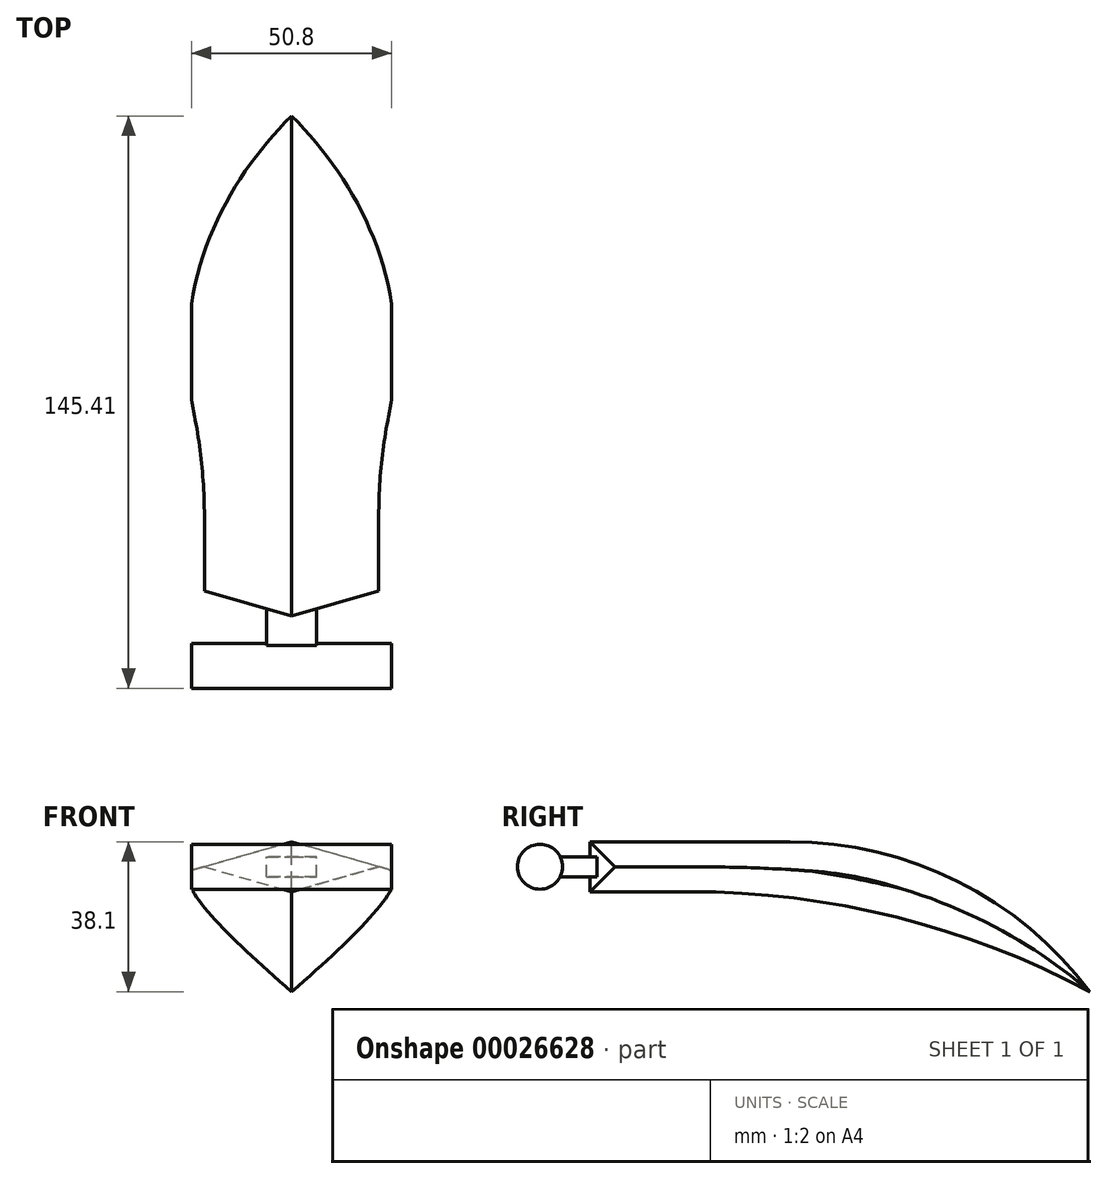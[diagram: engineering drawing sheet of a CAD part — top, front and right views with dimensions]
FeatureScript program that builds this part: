
annotation { "Feature Type Name" : "Feature", "Feature Type Description" : "" }
export const myFeature = defineFeature(function(context is Context, id is Id, definition is map)
    precondition{}
    {
        {
            var Q0;
            Q0=qCreatedBy(makeId("Front.planeOp"),FACE);
            var sketch = newSketch(context, id + "F0", { "sketchPlane" : qUnion([Q0])});
            skLineSegment(sketch, "E0.bottom", {"start": v(0, 0) * mm, "end": v(50.8, 0) * mm});
            skLineSegment(sketch, "E0.top", {"start": v(0, 50.8) * mm, "end": v(50.8, 50.8) * mm});
            skLineSegment(sketch, "E0.left", {"start": v(0, 0) * mm, "end": v(0, 50.8) * mm});
            skLineSegment(sketch, "E0.right", {"start": v(50.8, 0) * mm, "end": v(50.8, 50.8) * mm});
            skSolve(sketch);
        }
        {
            var Q0;
            Q0=qSketchRegion(id+"F0",true);
            extrude(context, id + "F1", {"entities" : qUnion([Q0]), "depth" : 50.8 * mm});
        }
        {
            var Q0;
            Q0=makeQuery(id+"F1.opExtrude","SWEPT_FACE",FACE,{"disambiguationData":[OSD([sQuery(id+"F0.wireOp",EDGE,"E0.bottom")])]});
            var Q1;
            Q1=makeQuery(id+"F1.opExtrude","SWEPT_FACE",FACE,{"disambiguationData":[OSD([sQuery(id+"F0.wireOp",EDGE,"E0.left")])]});
            var Q2;
            Q2=makeQuery(id+"F1.opExtrude","SWEPT_FACE",FACE,{"disambiguationData":[OSD([sQuery(id+"F0.wireOp",EDGE,"E0.top")])]});
            var Q3;
            Q3=makeQuery(id+"F1.opExtrude","SWEPT_FACE",FACE,{"disambiguationData":[OSD([sQuery(id+"F0.wireOp",EDGE,"E0.right")])]});
            fillet(context, id + "F2", {"entities" : qUnion([Q0, Q1, Q2, Q3]), "radius" : 12.7 * mm, "tangentPropagation" : true, "allowEdgeOverflow" : false});
        }
        {
            var Q0;
            Q0=makeQuery(id+"F1.opExtrude","SWEPT_FACE",FACE,{"disambiguationData":[OSD([sQuery(id+"F0.wireOp",EDGE,"E0.right")])]});
            var Q1;
            Q1=makeQuery(id+"F1.opExtrude","SWEPT_FACE",FACE,{"disambiguationData":[OSD([sQuery(id+"F0.wireOp",EDGE,"E0.left")])]});
            cPlane(context, id + "F3", {"entities" : qUnion([Q0, Q1]), "cplaneType" : CPlaneType.MID_PLANE, "offset" : 152.4 * mm, "width" : 152.4 * mm, "height" : 152.4 * mm});
        }
        {
            var Q0;
            Q0=makeQuery(id+"F1.opExtrude","CAP_FACE",FACE,{"disambiguationData":[OSD([sQuery(id+"F0.wireOp",EDGE,"E0.bottom"),sQuery(id+"F0.wireOp",EDGE,"E0.top"),sQuery(id+"F0.wireOp",EDGE,"E0.left"),sQuery(id+"F0.wireOp",EDGE,"E0.right")])],"isStart":false});
            var sketch = newSketch(context, id + "F4", { "sketchPlane" : qUnion([Q0])});
            skCircle(sketch, "E1", {"center": v(25.4, 25.4) * mm, "radius": 6.35 * mm});
            skSolve(sketch);
        }
        {
            var Q0;
            Q0=qSketchRegion(id+"F4",true);
            extrude(context, id + "F5", {"entities" : qUnion([Q0]), "operationType" : NewBodyOperationType.ADD, "depth" : 12.7 * mm});
        }
        {
            var Q0;
            Q0=qCreatedBy(id+"F3.planeOp",FACE);
            var sketch = newSketch(context, id + "F6", { "sketchPlane" : qUnion([Q0])});
            skPoint(sketch, "E2", {"position": v(-76.2, 25.4) * mm});
            skArc(sketch, "E3", {"start": v(-93.98, 25.4) * mm, "mid": v(-76.2, 7.62) * mm, "end": v(-58.42, 25.4) * mm});
            skLineSegment(sketch, "E4", {"start": v(-76.2, 25.4) * mm, "end": v(-58.42, 25.4) * mm});
            skLineSegment(sketch, "E5", {"start": v(-76.2, 25.4) * mm, "end": v(-93.98, 25.4) * mm});
            skSolve(sketch);
        }
        {
            var Q0;
            Q0=makeQuery(id+"F6.imprint","IMPRINT",FACE,{"disambiguationData":[TD([[makeQuery(id+"F6.imprint","IMPRINT",EDGE,{"derivedFrom":sQuery(id+"F6.wireOp",EDGE,"E3")}),1.0]])]});
            var Q1;
            Q1=sQuery(id+"F6.wireOp",EDGE,"E5");
            revolve(context, id + "F7", {"operationType" : NewBodyOperationType.ADD, "entities" : qUnion([Q0]), "axis" : qUnion([Q1]), "revolveType" : RevolveType.FULL});
        }
        {
            var Q0;
            Q0=qCreatedBy(id+"F3.planeOp",FACE);
            var sketch = newSketch(context, id + "F8", { "sketchPlane" : qUnion([Q0])});
            skLineSegment(sketch, "E6", {"start": v(-12.56, 38.02) * mm, "end": v(12.84, 38.02) * mm});
            skArc(sketch, "E7", {"start": v(12.84, 38.02) * mm, "mid": v(65.2, 31.57) * mm, "end": v(114.44, 12.62) * mm});
            skLineSegment(sketch, "E8", {"start": v(-12.56, 38.02) * mm, "end": v(-12.56, 50.72) * mm});
            skLineSegment(sketch, "E9", {"start": v(-12.56, 50.72) * mm, "end": v(38.24, 50.72) * mm});
            skArc(sketch, "E10", {"start": v(38.24, 50.72) * mm, "mid": v(80.84, 40.66) * mm, "end": v(114.44, 12.62) * mm});
            skSolve(sketch);
        }
        {
            var Q0;
            Q0=makeQuery(id+"F8.imprint","IMPRINT",FACE,{"disambiguationData":[TD([[makeQuery(id+"F8.imprint","IMPRINT",EDGE,{"derivedFrom":sQuery(id+"F8.wireOp",EDGE,"E6")}),1.0]])]});
            extrude(context, id + "F9", {"entities" : qUnion([Q0]), "depth" : 25.4 * mm, "hasDraft" : true, "draftAngle" : 16 * degree, "draftPullDirection" : true, "hasSecondDirection" : true, "secondDirectionOppositeDirection" : true, "secondDirectionDepth" : 25.4 * mm, "hasSecondDirectionDraft" : true, "secondDirectionDraftAngle" : 16 * degree, "secondDirectionDraftPullDirection" : true});
        }
        {
            var Q0;
            Q0=makeQuery(id+"F1.opExtrude","SWEPT_BODY",BODY,{"disambiguationData":[OSD([sQuery(id+"F0.wireOp",EDGE,"E0.bottom"),sQuery(id+"F0.wireOp",EDGE,"E0.top"),sQuery(id+"F0.wireOp",EDGE,"E0.left"),sQuery(id+"F0.wireOp",EDGE,"E0.right")])]});
            deleteBodies(context, id + "F10", {"entities" : qUnion([Q0])});
        }
        {
            var Q0;
            Q0=qCreatedBy(id+"F3.planeOp",FACE);
            var sketch = newSketch(context, id + "F11", { "sketchPlane" : qUnion([Q0])});
            skLineSegment(sketch, "E11", {"start": v(-12.56, 44.37) * mm, "end": v(-25.26, 44.37) * mm});
            skCircle(sketch, "E12", {"center": v(-25.26, 44.37) * mm, "radius": 5.72 * mm});
            skLineSegment(sketch, "E13.rect.bottom", {"start": v(-10.39, 41.83) * mm, "end": v(-23.09, 41.83) * mm});
            skLineSegment(sketch, "E13.rect.top", {"start": v(-10.39, 46.9) * mm, "end": v(-23.09, 46.9) * mm});
            skLineSegment(sketch, "E13.rect.left", {"start": v(-10.39, 41.83) * mm, "end": v(-10.39, 46.9) * mm});
            skLineSegment(sketch, "E13.rect.right", {"start": v(-23.09, 41.83) * mm, "end": v(-23.09, 46.9) * mm});
            skPoint(sketch, "E13.rect.middle", {"position": v(-16.74, 44.37) * mm});
            skSolve(sketch);
        }
        {
            var Q0;
            Q0=makeQuery(id+"F11.imprint","IMPRINT",FACE,{"disambiguationData":[TD([[makeQuery(id+"F11.imprint","IMPRINT",EDGE,{"derivedFrom":sQuery(id+"F11.wireOp",EDGE,"E12")}),1.0]])]});
            var Q1;
            {var subQ2=sQuery(id+"F11.wireOp",EDGE,"E13.rect.top");var subQ6=sQuery(id+"F11.wireOp",EDGE,"E12");var subQ7=makeQuery(id+"F11.imprint","INTERSECT",VERTEX,{"derivedFrom":[subQ6,subQ2]});Q1=makeQuery(id+"F11.imprint","IMPRINT",FACE,{"disambiguationData":[TD([[makeQuery(id+"F11.imprint","IMPRINT",EDGE,{"disambiguationData":[TD([[subQ7,-1.0]])],"derivedFrom":subQ6}),1.0]])]});}
            extrude(context, id + "F12", {"entities" : qUnion([Q0, Q1]), "depth" : 25.4 * mm, "hasSecondDirection" : true, "secondDirectionOppositeDirection" : true, "secondDirectionDepth" : 25.4 * mm});
        }
        {
            var Q0;
            {var subQ0=sQuery(id+"F11.wireOp",EDGE,"E13.rect.left");Q0=makeQuery(id+"F11.imprint","IMPRINT",FACE,{"disambiguationData":[TD([[makeQuery(id+"F11.imprint","IMPRINT",EDGE,{"derivedFrom":subQ0}),1.0]])]});}
            extrude(context, id + "F13", {"entities" : qUnion([Q0]), "operationType" : NewBodyOperationType.ADD, "depth" : 6.35 * mm, "hasSecondDirection" : true, "secondDirectionOppositeDirection" : true, "secondDirectionDepth" : 6.35 * mm});
        }
    });
